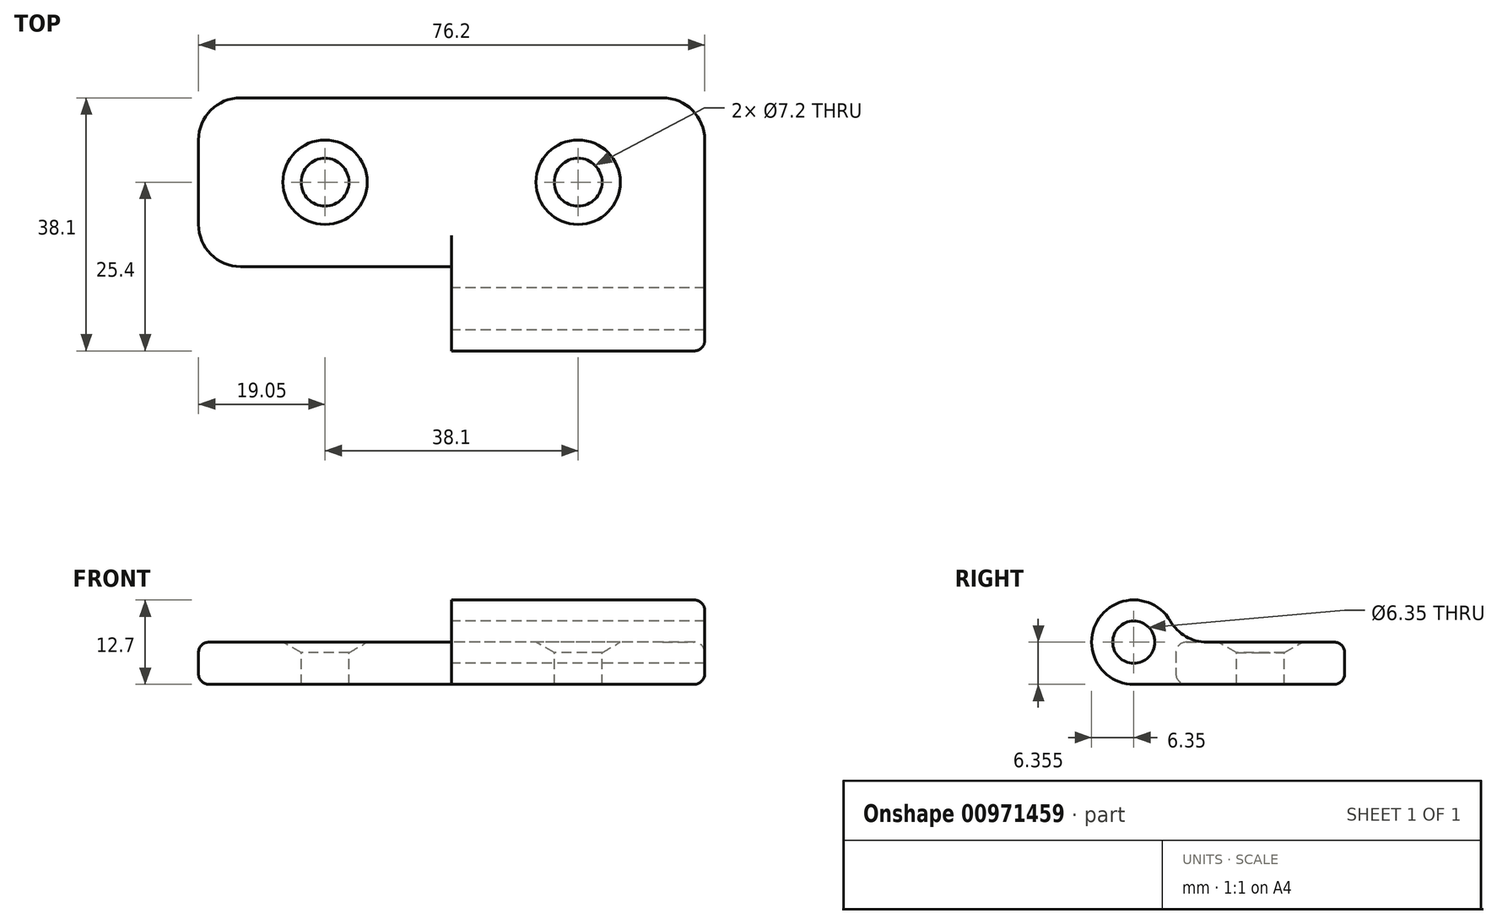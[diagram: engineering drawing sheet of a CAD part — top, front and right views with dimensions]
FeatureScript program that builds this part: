
annotation { "Feature Type Name" : "Feature", "Feature Type Description" : "" }
export const myFeature = defineFeature(function(context is Context, id is Id, definition is map)
    precondition{}
    {
        {
            var Q0;
            Q0=qCreatedBy(makeId("Right.planeOp"),FACE);
            var sketch = newSketch(context, id + "F0", { "sketchPlane" : qUnion([Q0])});
            skLineSegment(sketch, "E0.bottom", {"start": v(12.7, 3.18) * mm, "end": v(-8.05, 3.18) * mm});
            skLineSegment(sketch, "E0.top", {"start": v(12.7, -3.18) * mm, "end": v(-19.05, -3.18) * mm});
            skLineSegment(sketch, "E0.left", {"start": v(12.7, 3.18) * mm, "end": v(12.7, -3.18) * mm});
            skPoint(sketch, "E0.middle", {"position": v(0, 0) * mm});
            skArc(sketch, "E1", {"start": v(-13.55, 6.35) * mm, "mid": v(-24.55, 6.35) * mm, "end": v(-19.05, -3.17) * mm});
            skPoint(sketch, "E2.visualSharp", {"position": v(-12.7, 3.18) * mm});
            skArc(sketch, "E2.filletArc", {"start": v(-13.55, 6.35) * mm, "mid": v(-11.23, 4.03) * mm, "end": v(-8.05, 3.18) * mm});
            skCircle(sketch, "E3", {"center": v(-19.05, 3.18) * mm, "radius": 3.18 * mm});
            skSolve(sketch);
        }
        {
            var Q0;
            Q0 = qSketchRegion(id + "F0", true);
            extrude(context, id + "F1", {"entities" : qUnion([Q0]), "depth" : 38.1 * mm, "offsetDistance" : 25.4 * mm});
        }
        {
            var Q0;
            Q0=qCreatedBy(makeId("Right.planeOp"),FACE);
            var sketch = newSketch(context, id + "F2", { "sketchPlane" : qUnion([Q0])});
            skLineSegment(sketch, "E4.0", {"start": v(12.7, 3.18) * mm, "end": v(12.7, -3.18) * mm});
            skLineSegment(sketch, "E5.MirrorCS", {"start": v(-12.7, 3.18) * mm, "end": v(-12.7, -3.18) * mm});
            skLineSegment(sketch, "E6", {"start": v(12.7, 3.18) * mm, "end": v(-12.7, 3.18) * mm});
            skLineSegment(sketch, "E7", {"start": v(-12.7, -3.18) * mm, "end": v(12.7, -3.18) * mm});
            skSolve(sketch);
        }
        {
            var Q0;
            Q0 = qSketchRegion(id + "F2", true);
            extrude(context, id + "F3", {"entities" : qUnion([Q0]), "operationType" : NewBodyOperationType.ADD, "oppositeDirection" : true, "depth" : 38.1 * mm, "offsetDistance" : 25.4 * mm});
        }
        {
            var Q0;
            Q0=makeQuery(id+"F3.boolean.opBoolean","MERGE",FACE,{"derivedFrom":[makeQuery(id+"F1.opExtrude","SWEPT_FACE",FACE,{"disambiguationData":[OSD([sQuery(id+"F0.wireOp",EDGE,"E0.bottom")])]}),makeQuery(id+"F3.opExtrude","SWEPT_FACE",FACE,{"disambiguationData":[OSD([sQuery(id+"F2.wireOp",EDGE,"m7FQO3OU-lRbL-ETn8-z1tj-DBUO30yEYEnd.bottom")])]})]});
            var sketch = newSketch(context, id + "F4", { "sketchPlane" : qUnion([Q0])});
            skCircle(sketch, "E8", {"center": v(19.05, 0) * mm, "radius": 6.35 * mm});
            skCircle(sketch, "E9.MirrorC", {"center": v(-19.05, 0) * mm, "radius": 6.35 * mm});
            skSolve(sketch);
        }
        {
            var Q0;
            Q0 = qSketchRegion(id + "F4", true);
            extrude(context, id + "F5", {"entities" : qUnion([Q0]), "operationType" : NewBodyOperationType.REMOVE, "oppositeDirection" : true, "depth" : 1.59 * mm, "offsetDistance" : 25.4 * mm, "hasDraft" : true, "draftAngle" : 60 * degree, "draftPullDirection" : true});
        }
        {
            var Q0;
            Q0=makeQuery(id+"F5.boolean.opBoolean","COPY",FACE,{"derivedFrom":makeQuery(id+"F5.opExtrude","CAP_FACE",FACE,{"disambiguationData":[OSD([sQuery(id+"F4.wireOp",EDGE,"E8")])],"isStart":false})});
            var sketch = newSketch(context, id + "F6", { "sketchPlane" : qUnion([Q0])});
            skCircle(sketch, "E10.0", {"center": v(19.05, 0) * mm, "radius": 3.6 * mm});
            skCircle(sketch, "E11.0", {"center": v(-19.05, 0) * mm, "radius": 3.6 * mm});
            skSolve(sketch);
        }
        {
            var Q0;
            Q0 = qSketchRegion(id + "F6", true);
            extrude(context, id + "F7", {"entities" : qUnion([Q0]), "operationType" : NewBodyOperationType.REMOVE, "endBound" : BoundingType.THROUGH_ALL, "oppositeDirection" : true, "depth" : 25.4 * mm, "offsetDistance" : 25.4 * mm});
        }
        {
            var Q0;
            Q0=makeQuery(id+"F1.opExtrude","CAP_EDGE",EDGE,{"disambiguationData":[OSD([sQuery(id+"F0.wireOp",EDGE,"E0.left")])],"isStart":false});
            var Q1;
            Q1=makeQuery(id+"F3.opExtrude","CAP_EDGE",EDGE,{"disambiguationData":[OSD([sQuery(id+"F2.wireOp",EDGE,"E4.0")])],"isStart":false});
            var Q2;
            Q2=makeQuery(id+"F3.opExtrude","CAP_EDGE",EDGE,{"disambiguationData":[OSD([sQuery(id+"F2.wireOp",EDGE,"E5.MirrorCS")])],"isStart":false});
            fillet(context, id + "F8", {"entities" : qUnion([Q0, Q1, Q2]), "radius" : 6.35 * mm, "tangentPropagation" : true, "allowEdgeOverflow" : false});
        }
        {
            var Q0;
            Q0=makeQuery(id+"F3.boolean.opBoolean","MERGE",EDGE,{"derivedFrom":[makeQuery(id+"F1.opExtrude","SWEPT_EDGE",EDGE,{"disambiguationData":[OSD([sQuery(id+"F0.wireOp",EDGE,"E0.bottom"),sQuery(id+"F0.wireOp",EDGE,"E0.left")])]}),makeQuery(id+"F3.opExtrude","SWEPT_EDGE",EDGE,{"disambiguationData":[OSD([sQuery(id+"F2.wireOp",EDGE,"E4.0"),sQuery(id+"F2.wireOp",EDGE,"E6")])]})]});
            var Q1;
            Q1=makeQuery(id+"F8.opFillet","BLEND_EDGE",EDGE,{"blendedFrom":[makeQuery(id+"F1.opExtrude","CAP_EDGE",EDGE,{"disambiguationData":[OSD([sQuery(id+"F0.wireOp",EDGE,"E0.left")])],"isStart":false}),makeQuery(id+"F3.boolean.opBoolean","MERGE",FACE,{"derivedFrom":[makeQuery(id+"F1.opExtrude","SWEPT_FACE",FACE,{"disambiguationData":[OSD([sQuery(id+"F0.wireOp",EDGE,"E0.bottom")])]}),makeQuery(id+"F3.opExtrude","SWEPT_FACE",FACE,{"disambiguationData":[OSD([sQuery(id+"F2.wireOp",EDGE,"E6")])]})]})],"blendedInto":[makeQuery(id+"F3.boolean.opBoolean","MERGE",FACE,{"derivedFrom":[makeQuery(id+"F1.opExtrude","SWEPT_FACE",FACE,{"disambiguationData":[OSD([sQuery(id+"F0.wireOp",EDGE,"E0.bottom")])]}),makeQuery(id+"F3.opExtrude","SWEPT_FACE",FACE,{"disambiguationData":[OSD([sQuery(id+"F2.wireOp",EDGE,"E6")])]})]})]});
            fillet(context, id + "F9", {"entities" : qUnion([Q0, Q1]), "radius" : 1.59 * mm, "tangentPropagation" : true, "allowEdgeOverflow" : false});
        }
    });
